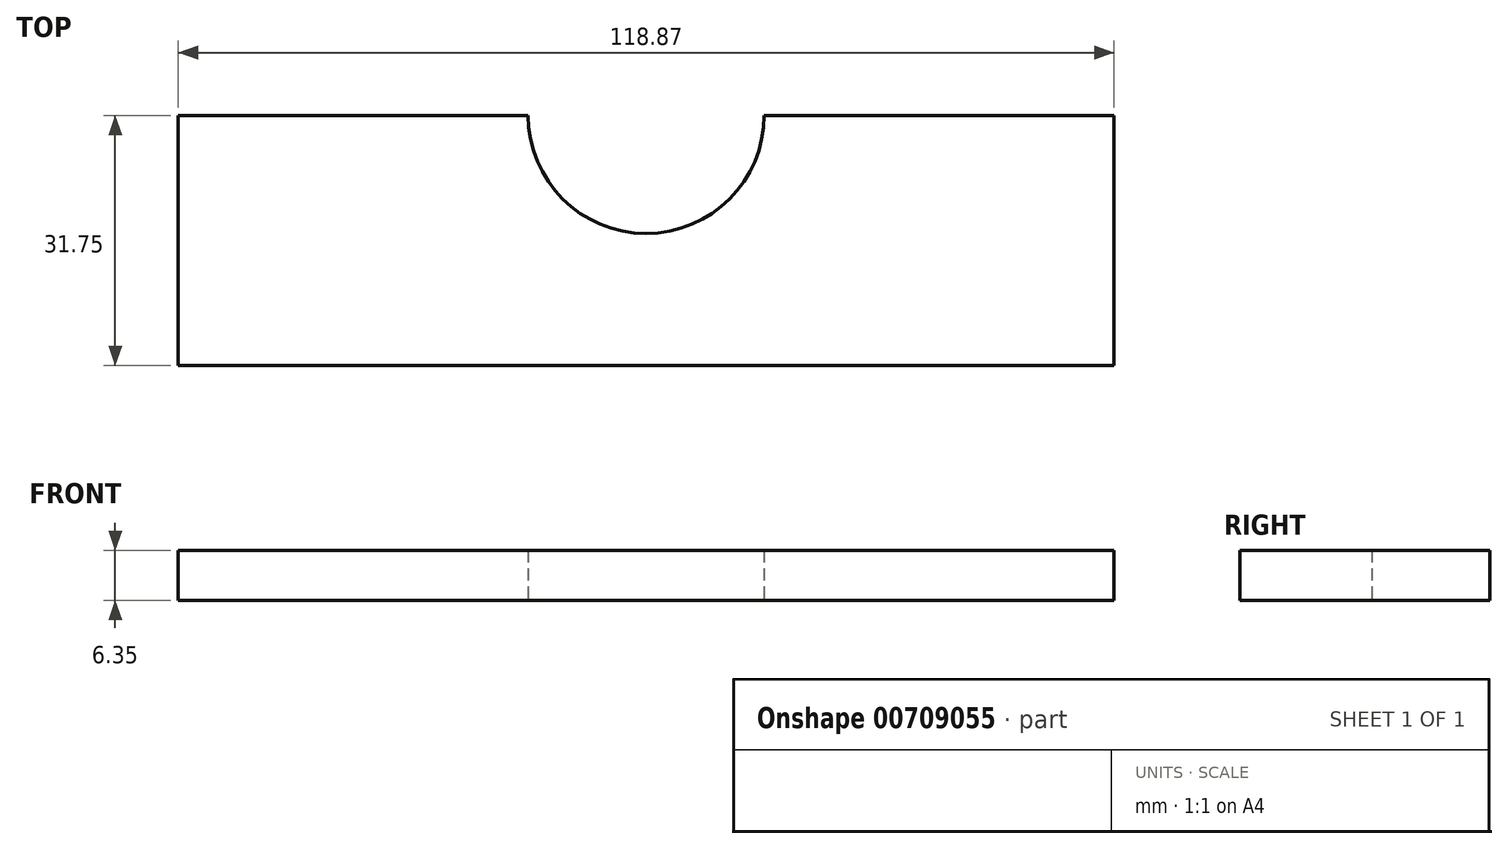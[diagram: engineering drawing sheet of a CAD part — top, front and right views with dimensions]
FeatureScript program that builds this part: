
annotation { "Feature Type Name" : "Feature", "Feature Type Description" : "" }
export const myFeature = defineFeature(function(context is Context, id is Id, definition is map)
    precondition{}
    {
        {
            var Q0;
            Q0=qCreatedBy(makeId("Top.planeOp"),FACE);
            var sketch = newSketch(context, id + "F0", { "sketchPlane" : qUnion([Q0])});
            skLineSegment(sketch, "E0.bottom", {"start": v(0, 0) * mm, "end": v(44.45, 0) * mm});
            skLineSegment(sketch, "E0.top", {"start": v(0, -31.75) * mm, "end": v(118.87, -31.75) * mm});
            skLineSegment(sketch, "E0.left", {"start": v(0, 0) * mm, "end": v(0, -31.75) * mm});
            skLineSegment(sketch, "E0.right", {"start": v(118.87, 0) * mm, "end": v(118.87, -31.75) * mm});
            skArc(sketch, "E1", {"start": v(44.45, 0) * mm, "mid": v(59.44, -14.99) * mm, "end": v(74.42, 0) * mm});
            skLineSegment(sketch, "E2.trimOffspring", {"start": v(74.42, 0) * mm, "end": v(118.87, 0) * mm});
            skSolve(sketch);
        }
        {
            var Q0;
            Q0=makeQuery(id+"F0.imprint","IMPRINT",FACE,{"disambiguationData":[TD([[makeQuery(id+"F0.imprint","IMPRINT",EDGE,{"derivedFrom":sQuery(id+"F0.wireOp",EDGE,"E0.bottom")}),-1.0]])]});
            extrude(context, id + "F1", {"entities" : qUnion([Q0]), "depth" : 6.35 * mm, "offsetDistance" : 25.4 * mm});
        }
    });
